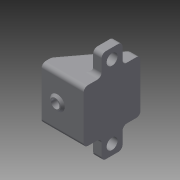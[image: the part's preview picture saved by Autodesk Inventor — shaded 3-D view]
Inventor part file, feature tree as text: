
AUTODESK INVENTOR PART (.ipt)
format: ipt  version: 2015 (Build 190159000, 159)  size: 220,160 bytes
history: native  units: mm
features: sketch x8, extrude x4, fillet x4, hole x2, plane x2, mirror x2, projected_geometry x2, loft x1, chamfer x1
ambient origin geometry x8: Origin, YZ Plane, XZ Plane, XY Plane, X Axis, Y Axis, Z Axis, Center Point
bodies: Solid1 (feature_tree)
feature tree (26):
  extrude  "Extrusion1"  Depth=25.0mm
  extrude  "Extrusion2"  Depth=5.0mm
  hole  "Hole1"  [1 undecoded]
  sketch  "Sketch4"  dims[d7=4.0mm d8=6.0mm d9=10.1mm d10=4.5mm d11=90.0deg d12=8.0mm d13=20.594885mm d14=5.0mm]
  plane  "Work Plane1"
  loft  "Loft1"
  fillet  "Fillet1"  [1 undecoded]
  mirror  "Mirror1"
  fillet  "Fillet2"  Radius=2.0mm
  extrude  "Extrusion3"  Depth=7.0mm
  chamfer  "Chamfer1"  Distance=1.0mm
  extrude  "Extrusion4"  Depth=4.0mm TaperAngle=0.0deg
  fillet  "Fillet3"  Radius=10.0mm
  hole  "Hole2"  [1 undecoded]
  plane  "Work Plane2"
  mirror  "Mirror2"
  fillet  "Fillet4"  Radius=2.0mm
  sketch  "Sketch1"  dims[d0=20.0mm d1=25.0mm]
  sketch  "Sketch2"  dims[d2=7.0mm d3=0.0mm d4=5.0mm]
  sketch  "Sketch3"  dims[d5=20.0mm d6=0.0mm]
  projected_geometry  "Projected Loop1"
  projected_geometry  "Projected Loop2"
  sketch  "Sketch5"  dims[d15=5.0mm d16=0.0mm d17=90.0deg d18=0.0mm d19=90.0deg d20=2.0mm]
  sketch  "Sketch6"  dims[d21=2.0mm d22=7.0mm d23=1.0mm d24=0.0mm]
  sketch  "Sketch7"  dims[d25=1.0mm d26=2.0mm d27=45.0deg d28=4.0mm d29=0.0mm d30=10.0mm]
  sketch  "Sketch8"  dims[d31=11.0mm d32=2.0mm d33=5.2mm d34=6.0mm d35=7.1mm d36=4.0mm d37=90.0deg d38=8.0mm d39=20.594885mm d40=2.0mm]
note: 3 required parameter values undecoded (feature->parameter linkage not recoverable at this tier; creation-order binding heuristic only, values carry confidence <= 0.55)
